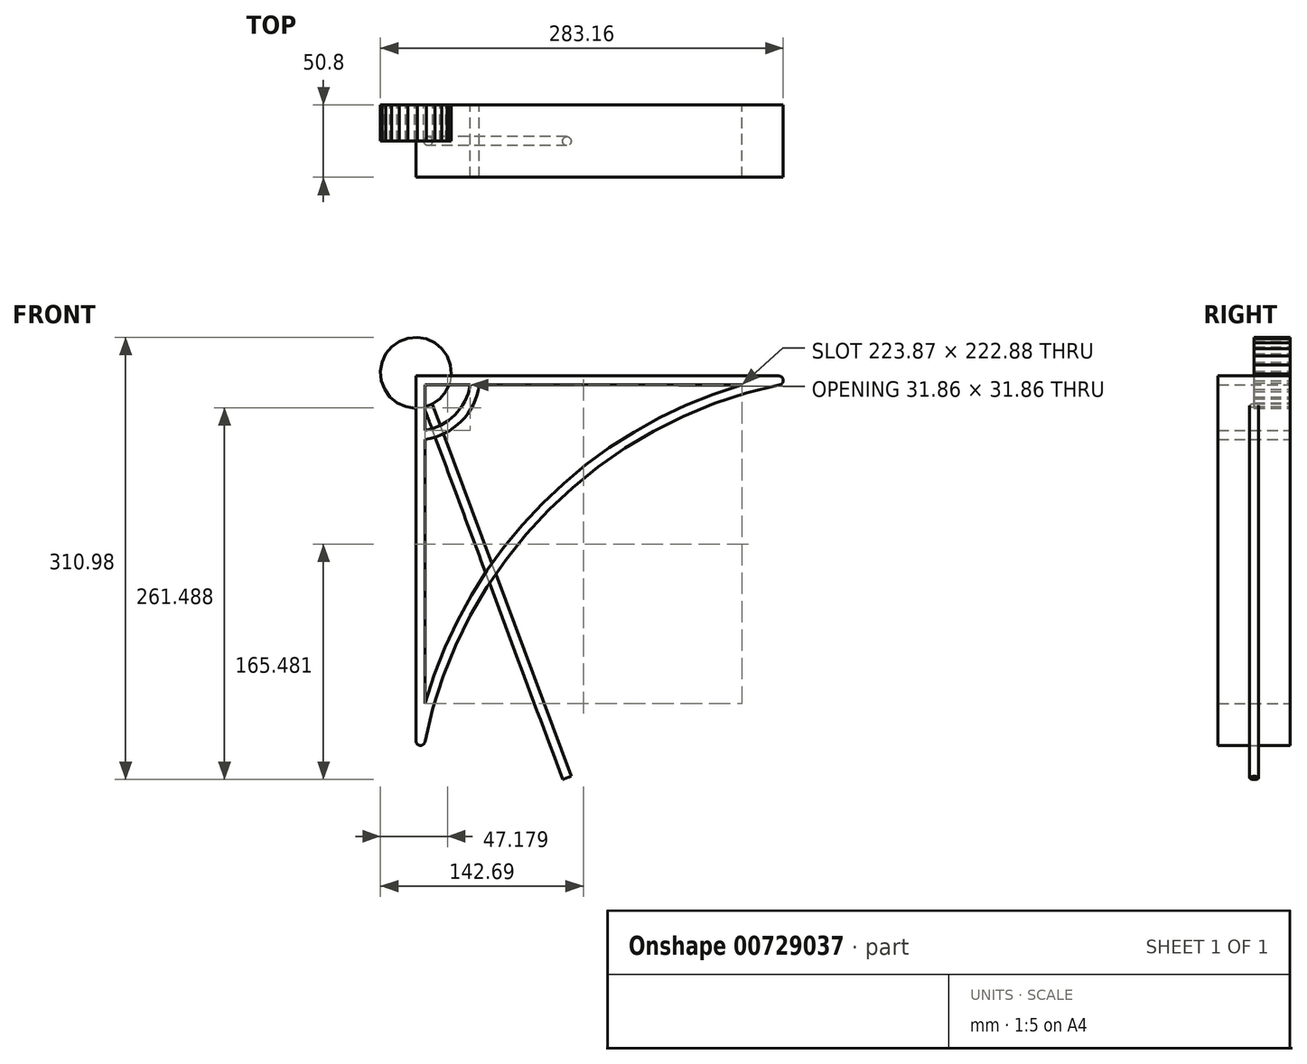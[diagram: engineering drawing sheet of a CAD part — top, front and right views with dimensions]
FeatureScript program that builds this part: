
annotation { "Feature Type Name" : "Feature", "Feature Type Description" : "" }
export const myFeature = defineFeature(function(context is Context, id is Id, definition is map)
    precondition{}
    {
        {
            var Q0;
            Q0=qCreatedBy(makeId("Front.planeOp"),FACE);
            var sketch = newSketch(context, id + "F0", { "sketchPlane" : qUnion([Q0])});
            skLineSegment(sketch, "E0", {"start": v(0, 63.84) * mm, "end": v(0, 320.5) * mm});
            skLineSegment(sketch, "E1", {"start": v(0, 320.5) * mm, "end": v(255.09, 320.5) * mm});
            skArc(sketch, "E2", {"start": v(255.73, 314.22) * mm, "mid": v(93.29, 226.2) * mm, "end": v(6.29, 63.21) * mm});
            skArc(sketch, "E3", {"start": v(6.35, 282.3) * mm, "mid": v(27.39, 293.12) * mm, "end": v(38.2, 314.16) * mm});
            skLineSegment(sketch, "E4.0", {"start": v(6.35, 314.16) * mm, "end": v(229.23, 314.16) * mm});
            skLineSegment(sketch, "E4.1", {"start": v(6.35, 90.28) * mm, "end": v(6.35, 314.16) * mm});
            skArc(sketch, "E4.2", {"start": v(229.23, 314.16) * mm, "mid": v(88.99, 230.9) * mm, "end": v(6.35, 90.28) * mm});
            skArc(sketch, "E5.0", {"start": v(6.35, 275.87) * mm, "mid": v(31.88, 288.63) * mm, "end": v(44.63, 314.16) * mm});
            skPoint(sketch, "E6.visualSharp", {"position": v(304.8, 320.5) * mm});
            skArc(sketch, "E6.filletArc", {"start": v(255.73, 314.22) * mm, "mid": v(258.25, 317.66) * mm, "end": v(255.09, 320.5) * mm});
            skPoint(sketch, "E7.visualSharp", {"position": v(0, 0) * mm});
            skArc(sketch, "E7.filletArc", {"start": v(0, 63.84) * mm, "mid": v(2.86, 60.68) * mm, "end": v(6.29, 63.21) * mm});
            skSolve(sketch);
        }
        {
            var Q0;
            Q0=makeQuery(id+"F0.imprint","IMPRINT",FACE,{"disambiguationData":[TD([[makeQuery(id+"F0.imprint","IMPRINT",EDGE,{"derivedFrom":sQuery(id+"F0.wireOp",EDGE,"E0")}),-1.0]])]});
            var Q1;
            {var subQ0=sQuery(id+"F0.wireOp",EDGE,"E3");Q1=makeQuery(id+"F0.imprint","IMPRINT",FACE,{"disambiguationData":[TD([[makeQuery(id+"F0.imprint","IMPRINT",EDGE,{"derivedFrom":subQ0}),-1.0]])]});}
            extrude(context, id + "F1", {"entities" : qUnion([Q0, Q1]), "depth" : 50.8 * mm, "offsetDistance" : 25.4 * mm});
        }
        {
            var Q0;
            Q0=qCreatedBy(makeId("Front.planeOp"),FACE);
            var sketch = newSketch(context, id + "F2", { "sketchPlane" : qUnion([Q0])});
            skCircle(sketch, "E8.cCircle", {"center": v(0, 322.82) * mm, "radius": 24.7 * mm, "construction": true});
            skLineSegment(sketch, "E8.0", {"start": v(22.01, 334.5) * mm, "end": v(24.28, 328.4) * mm});
            skLineSegment(sketch, "E8.1", {"start": v(24.28, 328.4) * mm, "end": v(24.9, 321.92) * mm});
            skLineSegment(sketch, "E8.2", {"start": v(24.9, 321.92) * mm, "end": v(23.82, 315.51) * mm});
            skLineSegment(sketch, "E8.3", {"start": v(23.82, 315.51) * mm, "end": v(21.11, 309.6) * mm});
            skLineSegment(sketch, "E8.4", {"start": v(21.11, 309.6) * mm, "end": v(16.97, 304.58) * mm});
            skLineSegment(sketch, "E8.5", {"start": v(16.97, 304.58) * mm, "end": v(11.67, 300.81) * mm});
            skLineSegment(sketch, "E8.6", {"start": v(11.67, 300.81) * mm, "end": v(5.57, 298.54) * mm});
            skLineSegment(sketch, "E8.7", {"start": v(5.57, 298.54) * mm, "end": v(-0.9, 297.93) * mm});
            skLineSegment(sketch, "E8.8", {"start": v(-0.9, 297.93) * mm, "end": v(-7.31, 299) * mm});
            skLineSegment(sketch, "E8.9", {"start": v(-7.31, 299) * mm, "end": v(-13.23, 301.71) * mm});
            skLineSegment(sketch, "E8.10", {"start": v(-13.23, 301.71) * mm, "end": v(-18.24, 305.86) * mm});
            skLineSegment(sketch, "E8.11", {"start": v(-18.24, 305.86) * mm, "end": v(-22.01, 311.15) * mm});
            skLineSegment(sketch, "E8.12", {"start": v(-22.01, 311.15) * mm, "end": v(-24.28, 317.25) * mm});
            skLineSegment(sketch, "E8.13", {"start": v(-24.28, 317.25) * mm, "end": v(-24.9, 323.72) * mm});
            skLineSegment(sketch, "E8.14", {"start": v(-24.9, 323.72) * mm, "end": v(-23.82, 330.14) * mm});
            skLineSegment(sketch, "E8.15", {"start": v(-23.82, 330.14) * mm, "end": v(-21.11, 336.05) * mm});
            skLineSegment(sketch, "E8.16", {"start": v(-21.11, 336.05) * mm, "end": v(-16.97, 341.06) * mm});
            skLineSegment(sketch, "E8.17", {"start": v(-16.97, 341.06) * mm, "end": v(-11.67, 344.83) * mm});
            skLineSegment(sketch, "E8.18", {"start": v(-11.67, 344.83) * mm, "end": v(-5.57, 347.1) * mm});
            skLineSegment(sketch, "E8.19", {"start": v(-5.57, 347.1) * mm, "end": v(0.9, 347.72) * mm});
            skLineSegment(sketch, "E8.20", {"start": v(0.9, 347.72) * mm, "end": v(7.31, 346.64) * mm});
            skLineSegment(sketch, "E8.21", {"start": v(7.31, 346.64) * mm, "end": v(13.23, 343.93) * mm});
            skLineSegment(sketch, "E8.22", {"start": v(13.23, 343.93) * mm, "end": v(18.24, 339.8) * mm});
            skLineSegment(sketch, "E8.23", {"start": v(18.24, 339.8) * mm, "end": v(22.01, 334.5) * mm});
            skPoint(sketch, "E8.0.midPoint", {"position": v(23.15, 331.45) * mm});
            skSolve(sketch);
        }
        {
            var Q0;
            Q0=makeQuery(id+"F2.imprint","IMPRINT",FACE,{"disambiguationData":[TD([[makeQuery(id+"F2.imprint","IMPRINT",EDGE,{"derivedFrom":sQuery(id+"F2.wireOp",EDGE,"E8.0")}),-1.0]])]});
            extrude(context, id + "F3", {"entities" : qUnion([Q0]), "depth" : 25.4 * mm, "offsetDistance" : 25.4 * mm});
        }
        {
            var Q0;
            Q0=makeQuery(id+"F3.opExtrude","SWEPT_FACE",FACE,{"disambiguationData":[OSD([sQuery(id+"F2.wireOp",EDGE,"E8.6")])]});
            var sketch = newSketch(context, id + "F4", { "sketchPlane" : qUnion([Q0])});
            skPoint(sketch, "E9.centerSnap0", {"position": v(109.43, 12.7) * mm});
            skCircle(sketch, "E10", {"center": v(112.69, 25.4) * mm, "radius": 3.18 * mm});
            skSolve(sketch);
        }
        {
            var Q0;
            Q0=makeQuery(id+"F3.opExtrude","SWEPT_FACE",FACE,{"disambiguationData":[OSD([sQuery(id+"F2.wireOp",EDGE,"E8.5")])]});
            var sketch = newSketch(context, id + "F5", { "sketchPlane" : qUnion([Q0])});
            skCircle(sketch, "E11", {"center": v(187.14, 25.4) * mm, "radius": 3.18 * mm});
            skSolve(sketch);
        }
        {
            var Q0;
            {var subQ0=sQuery(id+"F4.wireOp",EDGE,"E10");var subQ1=makeQuery(id+"F3.opExtrude","CAP_EDGE",EDGE,{"disambiguationData":[OSD([sQuery(id+"F2.wireOp",EDGE,"E8.6")])],"isStart":false});var subQ2=makeQuery(id+"F4.imprint","INTERSECT",VERTEX,{"disambiguationData":[OD(0.0)],"derivedFrom":[subQ1,subQ0]});Q0=makeQuery(id+"F4.imprint","IMPRINT",FACE,{"disambiguationData":[TD([[makeQuery(id+"F4.imprint","IMPRINT",EDGE,{"disambiguationData":[TD([[subQ2,-1.0]])],"derivedFrom":subQ0}),1.0]])]});}
            var Q1;
            {var subQ0=sQuery(id+"F4.wireOp",EDGE,"E10");var subQ1=makeQuery(id+"F3.opExtrude","CAP_EDGE",EDGE,{"disambiguationData":[OSD([sQuery(id+"F2.wireOp",EDGE,"E8.6")])],"isStart":false});var subQ2=makeQuery(id+"F4.imprint","INTERSECT",VERTEX,{"disambiguationData":[OD(0.0)],"derivedFrom":[subQ1,subQ0]});Q1=makeQuery(id+"F4.imprint","IMPRINT",FACE,{"disambiguationData":[TD([[makeQuery(id+"F4.imprint","IMPRINT",EDGE,{"disambiguationData":[TD([[subQ2,1.0]])],"derivedFrom":subQ0}),1.0]])]});}
            var Q2;
            Q2=sQuery(id+"F5.wireOp",EDGE,"E11");
            extrude(context, id + "F6", {"entities" : qUnion([Q0, Q1]), "surfaceEntities" : qUnion([Q2]), "depth" : 279.4 * mm, "offsetDistance" : 25.4 * mm});
        }
    });
